# Revit family: Cassette fibre optique à splicer pour panneau modulaire HD
name_source: partatom
category: Installations électriques
units: mm (PartAtom-declared; Revit-internal decimal feet)

## family parameters
Conserver l'orientation des annotations = Non
Cote de connecteur circulaire = Utiliser le diamètre
Couper avec des vides une fois chargée = Non
Hôte = Face
Partagée = Oui
Point de calcul de pièce = Non
Type d'élément = Normal

## types (1)
- Cassette fibre optique à splicer pour panneau modulaire HD
    Classe d'application = EC000762
    Conditions Générale d'Utilisation = https://export.legrand.com
    Description = Cassette fibre optique à splicer pour panneau modulaire HD
    EAN = 3414970962126
    Elévation par défaut = 1219 mm
    Fabricant = LEGRAND
    Fonction = Cassette fibre optique à splicer
    Hauteur (mm) = 44 mm
    Largeur (mm) = 110 mm
    Libellé BIM = Legrand FIBER PATCH PANELS
    Lien e-catalogue = https://www.legrand.fr
    Longueur = 185 mm  [stored 0.606955 ft]
    Référence Legrand = LG-032141

note: [stored X ft] marks values corroborated as IEEE doubles in the binary element streams (Revit-internal decimal feet)
